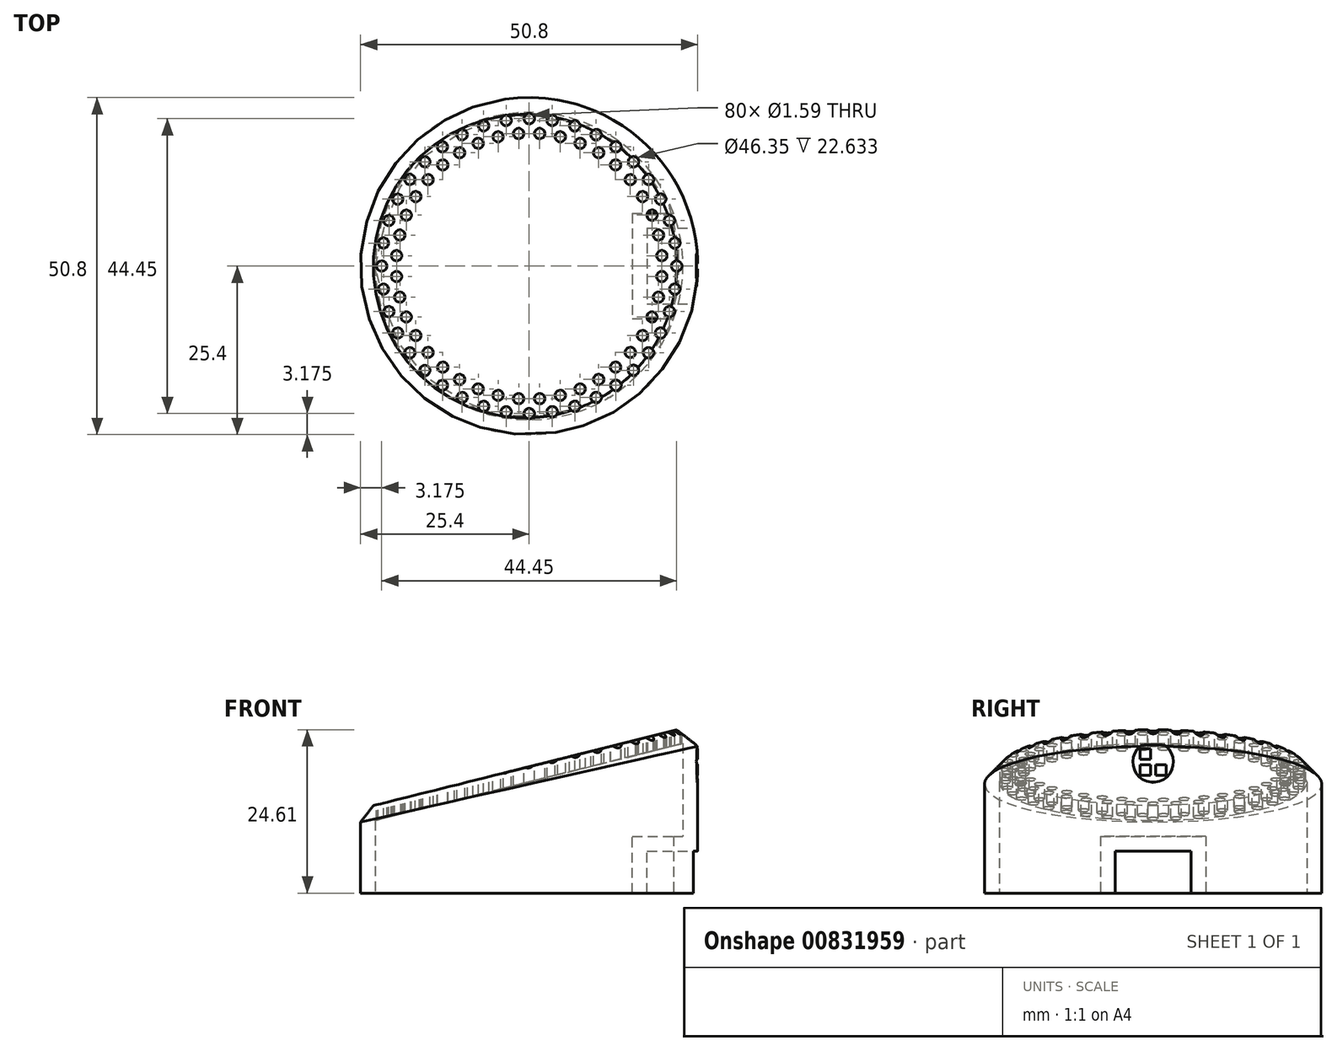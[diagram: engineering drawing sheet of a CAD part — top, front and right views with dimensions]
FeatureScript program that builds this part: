
annotation { "Feature Type Name" : "Feature", "Feature Type Description" : "" }
export const myFeature = defineFeature(function(context is Context, id is Id, definition is map)
    precondition{}
    {
        {
            var Q0;
            Q0=qCreatedBy(makeId("Front.planeOp"),FACE);
            var sketch = newSketch(context, id + "F0", { "sketchPlane" : qUnion([Q0])});
            skLineSegment(sketch, "E0", {"start": v(25.4, 0) * mm, "end": v(25.4, 25.4) * mm});
            skLineSegment(sketch, "E1", {"start": v(25.4, 25.4) * mm, "end": v(-25.4, 12.7) * mm});
            skLineSegment(sketch, "E2", {"start": v(-25.4, 12.7) * mm, "end": v(-25.4, 0) * mm});
            skLineSegment(sketch, "E3", {"start": v(-25.4, 0) * mm, "end": v(25.4, 0) * mm});
            skSolve(sketch);
        }
        {
            var Q0;
            Q0 = qSketchRegion(id + "F0", true);
            extrude(context, id + "F1", {"entities" : qUnion([Q0]), "endBound" : BoundingType.SYMMETRIC, "depth" : 50.8 * mm, "offsetDistance" : 25.4 * mm});
        }
        {
            var Q0;
            Q0=qCreatedBy(makeId("Top.planeOp"),FACE);
            var sketch = newSketch(context, id + "F2", { "sketchPlane" : qUnion([Q0])});
            skCircle(sketch, "E4", {"center": v(0, 0) * mm, "radius": 25.4 * mm});
            skLineSegment(sketch, "E5.bottom", {"start": v(25.4, -25.4) * mm, "end": v(-25.4, -25.4) * mm});
            skLineSegment(sketch, "E5.top", {"start": v(25.4, 25.4) * mm, "end": v(-25.4, 25.4) * mm});
            skLineSegment(sketch, "E5.left", {"start": v(25.4, -25.4) * mm, "end": v(25.4, 25.4) * mm});
            skLineSegment(sketch, "E5.right", {"start": v(-25.4, -25.4) * mm, "end": v(-25.4, 25.4) * mm});
            skSolve(sketch);
        }
        {
            var Q0;
            {var subQ0=sQuery(id+"F2.wireOp",EDGE,"E5.right");var subQ1=sQuery(id+"F2.wireOp",EDGE,"E4");var subQ2=makeQuery(id+"F2.imprint","INTERSECT",VERTEX,{"derivedFrom":[subQ1,subQ0]});Q0=makeQuery(id+"F2.imprint","IMPRINT",FACE,{"disambiguationData":[TD([[makeQuery(id+"F2.imprint","IMPRINT",EDGE,{"disambiguationData":[TD([[subQ2,-1.0]])],"derivedFrom":subQ1}),-1.0]])]});}
            var Q1;
            {var subQ0=sQuery(id+"F2.wireOp",EDGE,"E5.left");var subQ1=sQuery(id+"F2.wireOp",EDGE,"E4");var subQ2=makeQuery(id+"F2.imprint","INTERSECT",VERTEX,{"derivedFrom":[subQ1,subQ0]});Q1=makeQuery(id+"F2.imprint","IMPRINT",FACE,{"disambiguationData":[TD([[makeQuery(id+"F2.imprint","IMPRINT",EDGE,{"disambiguationData":[TD([[subQ2,1.0]])],"derivedFrom":subQ1}),-1.0]])]});}
            var Q2;
            {var subQ0=sQuery(id+"F2.wireOp",EDGE,"E5.top");var subQ1=sQuery(id+"F2.wireOp",EDGE,"E4");var subQ2=makeQuery(id+"F2.imprint","INTERSECT",VERTEX,{"derivedFrom":[subQ1,subQ0]});Q2=makeQuery(id+"F2.imprint","IMPRINT",FACE,{"disambiguationData":[TD([[makeQuery(id+"F2.imprint","IMPRINT",EDGE,{"disambiguationData":[TD([[subQ2,1.0]])],"derivedFrom":subQ1}),-1.0]])]});}
            var Q3;
            {var subQ0=sQuery(id+"F2.wireOp",EDGE,"E5.top");var subQ1=sQuery(id+"F2.wireOp",EDGE,"E4");var subQ2=makeQuery(id+"F2.imprint","INTERSECT",VERTEX,{"derivedFrom":[subQ1,subQ0]});Q3=makeQuery(id+"F2.imprint","IMPRINT",FACE,{"disambiguationData":[TD([[makeQuery(id+"F2.imprint","IMPRINT",EDGE,{"disambiguationData":[TD([[subQ2,-1.0]])],"derivedFrom":subQ1}),-1.0]])]});}
            extrude(context, id + "F3", {"entities" : qUnion([Q0, Q1, Q2, Q3]), "operationType" : NewBodyOperationType.REMOVE, "endBound" : BoundingType.THROUGH_ALL, "depth" : 76.2 * mm, "offsetDistance" : 25.4 * mm});
        }
        {
            var Q0;
            Q0=qCreatedBy(makeId("Right.planeOp"),FACE);
            cPlane(context, id + "F4", {"entities" : qUnion([Q0]), "cplaneType" : CPlaneType.OFFSET, "offset" : 25.4 * mm, "width" : 152.4 * mm, "height" : 152.4 * mm});
        }
        {
            var Q0;
            Q0=qCreatedBy(id+"F4.planeOp",FACE);
            var sketch = newSketch(context, id + "F5", { "sketchPlane" : qUnion([Q0])});
            skLineSegment(sketch, "E6.bottom", {"start": v(5.72, 0) * mm, "end": v(-5.72, 0) * mm});
            skLineSegment(sketch, "E6.top", {"start": v(5.72, 6.35) * mm, "end": v(-5.72, 6.35) * mm});
            skLineSegment(sketch, "E6.left", {"start": v(5.71, 0) * mm, "end": v(5.71, 6.35) * mm});
            skLineSegment(sketch, "E6.right", {"start": v(-5.72, 0) * mm, "end": v(-5.72, 6.35) * mm});
            skLineSegment(sketch, "E7", {"start": v(0, 0) * mm, "end": v(0, 6.35) * mm, "construction": true});
            skSolve(sketch);
        }
        {
            var Q0;
            Q0 = qSketchRegion(id + "F5", true);
            extrude(context, id + "F6", {"entities" : qUnion([Q0]), "operationType" : NewBodyOperationType.REMOVE, "oppositeDirection" : true, "depth" : 7.62 * mm, "offsetDistance" : 25.4 * mm});
        }
        {
            var Q0;
            Q0=makeQuery(id+"F1.opExtrude","SWEPT_FACE",FACE,{"disambiguationData":[OSD([sQuery(id+"F0.wireOp",EDGE,"E3")])]});
            cPlane(context, id + "F7", {"entities" : qUnion([Q0]), "cplaneType" : CPlaneType.OFFSET, "offset" : 25.4 * mm, "oppositeDirection" : true, "width" : 152.4 * mm, "height" : 152.4 * mm});
        }
        {
            var Q0;
            Q0=qCreatedBy(id+"F7.planeOp",FACE);
            var sketch = newSketch(context, id + "F8", { "sketchPlane" : qUnion([Q0])});
            skCircle(sketch, "E8", {"center": v(0, -22.23) * mm, "radius": 0.8 * mm});
            skLineSegment(sketch, "E9", {"start": v(0, 25.4) * mm, "end": v(0, -25.4) * mm, "construction": true});
            skCircle(sketch, "E10.1.0", {"center": v(3.48, -21.95) * mm, "radius": 0.8 * mm});
            skCircle(sketch, "E10.2.0", {"center": v(6.87, -21.14) * mm, "radius": 0.8 * mm});
            skCircle(sketch, "E10.3.0", {"center": v(10.09, -19.8) * mm, "radius": 0.8 * mm});
            skCircle(sketch, "E10.4.0", {"center": v(13.06, -17.98) * mm, "radius": 0.8 * mm});
            skCircle(sketch, "E10.5.0", {"center": v(15.72, -15.72) * mm, "radius": 0.8 * mm});
            skCircle(sketch, "E10.6.0", {"center": v(17.98, -13.06) * mm, "radius": 0.8 * mm});
            skCircle(sketch, "E10.7.0", {"center": v(19.8, -10.09) * mm, "radius": 0.8 * mm});
            skCircle(sketch, "E10.8.0", {"center": v(21.14, -6.87) * mm, "radius": 0.8 * mm});
            skCircle(sketch, "E10.9.0", {"center": v(21.95, -3.48) * mm, "radius": 0.8 * mm});
            skCircle(sketch, "E10.10.0", {"center": v(22.23, 0) * mm, "radius": 0.8 * mm});
            skCircle(sketch, "E10.11.0", {"center": v(21.95, 3.48) * mm, "radius": 0.8 * mm});
            skCircle(sketch, "E10.12.0", {"center": v(21.14, 6.87) * mm, "radius": 0.8 * mm});
            skCircle(sketch, "E10.13.0", {"center": v(19.8, 10.09) * mm, "radius": 0.8 * mm});
            skCircle(sketch, "E10.14.0", {"center": v(17.98, 13.06) * mm, "radius": 0.8 * mm});
            skCircle(sketch, "E10.15.0", {"center": v(15.72, 15.72) * mm, "radius": 0.8 * mm});
            skCircle(sketch, "E10.16.0", {"center": v(13.06, 17.98) * mm, "radius": 0.8 * mm});
            skCircle(sketch, "E10.17.0", {"center": v(10.09, 19.8) * mm, "radius": 0.8 * mm});
            skCircle(sketch, "E10.18.0", {"center": v(6.87, 21.14) * mm, "radius": 0.8 * mm});
            skCircle(sketch, "E10.19.0", {"center": v(3.48, 21.95) * mm, "radius": 0.8 * mm});
            skPoint(sketch, "E10.center", {"position": v(0, 0) * mm});
            skCircle(sketch, "E11.1.20.0", {"center": v(0, 22.23) * mm, "radius": 0.8 * mm});
            skCircle(sketch, "E11.1.21.0", {"center": v(-3.48, 21.95) * mm, "radius": 0.8 * mm});
            skCircle(sketch, "E11.1.22.0", {"center": v(-6.87, 21.14) * mm, "radius": 0.8 * mm});
            skCircle(sketch, "E11.1.23.0", {"center": v(-10.09, 19.8) * mm, "radius": 0.8 * mm});
            skCircle(sketch, "E11.1.24.0", {"center": v(-13.06, 17.98) * mm, "radius": 0.8 * mm});
            skCircle(sketch, "E11.1.25.0", {"center": v(-15.72, 15.72) * mm, "radius": 0.8 * mm});
            skCircle(sketch, "E11.1.26.0", {"center": v(-17.98, 13.06) * mm, "radius": 0.8 * mm});
            skCircle(sketch, "E11.1.27.0", {"center": v(-19.8, 10.09) * mm, "radius": 0.8 * mm});
            skCircle(sketch, "E11.1.28.0", {"center": v(-21.14, 6.87) * mm, "radius": 0.8 * mm});
            skCircle(sketch, "E11.1.29.0", {"center": v(-21.95, 3.48) * mm, "radius": 0.8 * mm});
            skCircle(sketch, "E11.1.30.0", {"center": v(-22.23, 0) * mm, "radius": 0.8 * mm});
            skCircle(sketch, "E11.1.31.0", {"center": v(-21.95, -3.48) * mm, "radius": 0.8 * mm});
            skCircle(sketch, "E11.1.32.0", {"center": v(-21.14, -6.87) * mm, "radius": 0.8 * mm});
            skCircle(sketch, "E11.1.33.0", {"center": v(-19.8, -10.09) * mm, "radius": 0.8 * mm});
            skCircle(sketch, "E11.1.34.0", {"center": v(-17.98, -13.06) * mm, "radius": 0.8 * mm});
            skCircle(sketch, "E11.1.35.0", {"center": v(-15.72, -15.72) * mm, "radius": 0.8 * mm});
            skCircle(sketch, "E11.1.36.0", {"center": v(-13.06, -17.98) * mm, "radius": 0.8 * mm});
            skCircle(sketch, "E11.1.37.0", {"center": v(-10.09, -19.8) * mm, "radius": 0.8 * mm});
            skCircle(sketch, "E11.1.38.0", {"center": v(-6.87, -21.14) * mm, "radius": 0.8 * mm});
            skCircle(sketch, "E11.1.39.0", {"center": v(-3.48, -21.95) * mm, "radius": 0.8 * mm});
            skSolve(sketch);
        }
        {
            var Q0;
            Q0=makeQuery(id+"F1.opExtrude","SWEPT_FACE",FACE,{"disambiguationData":[OSD([sQuery(id+"F0.wireOp",EDGE,"E3")])]});
            shell(context, id + "F9", {"entities" : qUnion([Q0]), "thickness" : 2.22 * mm});
        }
        {
            var Q0;
            Q0 = qSketchRegion(id + "F8", true);
            var Q1;
            Q1=makeQuery(id+"F9.opShell","OFFSET_FACE",FACE,{"disambiguationData":[OSD([sQuery(id+"F0.wireOp",EDGE,"E1")])]});
            var Q2;
            Q2=makeQuery(id+"F9.opShell","OFFSET_VERTEX",VERTEX,{"disambiguationData":[OSD([sQuery(id+"F5.wireOp",EDGE,"E6.top"),sQuery(id+"F5.wireOp",EDGE,"E6.right")])]});
            extrude(context, id + "F10", {"entities" : qUnion([Q0, Q1]), "operationType" : NewBodyOperationType.REMOVE, "endBound" : BoundingType.UP_TO_VERTEX, "depth" : 25.4 * mm, "endBoundEntityVertex" : qUnion([Q2]), "offsetDistance" : 25.4 * mm});
        }
        {
            var Q0;
            Q0=qCreatedBy(id+"F7.planeOp",FACE);
            var sketch = newSketch(context, id + "F11", { "sketchPlane" : qUnion([Q0])});
            skCircle(sketch, "E12", {"center": v(19.98, 1.57) * mm, "radius": 0.8 * mm});
            skLineSegment(sketch, "E13", {"start": v(0, 0) * mm, "end": v(22.23, 0) * mm, "construction": true});
            skLineSegment(sketch, "E14", {"start": v(21.95, 3.48) * mm, "end": v(0, 0) * mm, "construction": true});
            skLineSegment(sketch, "E15", {"start": v(21.95, 3.48) * mm, "end": v(22.23, 0) * mm, "construction": true});
            skLineSegment(sketch, "E16", {"start": v(22.09, 1.74) * mm, "end": v(0, 0) * mm, "construction": true});
            skCircle(sketch, "E17.1.0", {"center": v(19.49, 4.68) * mm, "radius": 0.8 * mm});
            skCircle(sketch, "E17.2.0", {"center": v(18.51, 7.67) * mm, "radius": 0.8 * mm});
            skPoint(sketch, "E17.center", {"position": v(0, 0) * mm});
            skCircle(sketch, "E18.1.3.0", {"center": v(17.09, 10.47) * mm, "radius": 0.8 * mm});
            skCircle(sketch, "E18.1.4.0", {"center": v(15.24, 13.01) * mm, "radius": 0.8 * mm});
            skCircle(sketch, "E18.1.5.0", {"center": v(13.01, 15.24) * mm, "radius": 0.8 * mm});
            skCircle(sketch, "E18.1.6.0", {"center": v(10.47, 17.09) * mm, "radius": 0.8 * mm});
            skCircle(sketch, "E18.1.7.0", {"center": v(7.67, 18.51) * mm, "radius": 0.8 * mm});
            skCircle(sketch, "E18.1.8.0", {"center": v(4.68, 19.49) * mm, "radius": 0.8 * mm});
            skCircle(sketch, "E18.1.9.0", {"center": v(1.57, 19.98) * mm, "radius": 0.8 * mm});
            skCircle(sketch, "E18.1.10.0", {"center": v(-1.57, 19.98) * mm, "radius": 0.8 * mm});
            skCircle(sketch, "E18.1.11.0", {"center": v(-4.68, 19.49) * mm, "radius": 0.8 * mm});
            skCircle(sketch, "E18.1.12.0", {"center": v(-7.67, 18.51) * mm, "radius": 0.8 * mm});
            skCircle(sketch, "E18.1.13.0", {"center": v(-10.47, 17.09) * mm, "radius": 0.8 * mm});
            skCircle(sketch, "E18.1.14.0", {"center": v(-13.01, 15.24) * mm, "radius": 0.8 * mm});
            skCircle(sketch, "E18.1.15.0", {"center": v(-15.24, 13.01) * mm, "radius": 0.8 * mm});
            skCircle(sketch, "E18.1.16.0", {"center": v(-17.09, 10.47) * mm, "radius": 0.8 * mm});
            skCircle(sketch, "E18.1.17.0", {"center": v(-18.51, 7.67) * mm, "radius": 0.8 * mm});
            skCircle(sketch, "E18.1.18.0", {"center": v(-19.49, 4.68) * mm, "radius": 0.8 * mm});
            skCircle(sketch, "E18.1.19.0", {"center": v(-19.98, 1.57) * mm, "radius": 0.8 * mm});
            skCircle(sketch, "E18.1.20.0", {"center": v(-19.98, -1.57) * mm, "radius": 0.8 * mm});
            skCircle(sketch, "E18.1.21.0", {"center": v(-19.49, -4.68) * mm, "radius": 0.8 * mm});
            skCircle(sketch, "E18.1.22.0", {"center": v(-18.51, -7.67) * mm, "radius": 0.8 * mm});
            skCircle(sketch, "E18.1.23.0", {"center": v(-17.09, -10.47) * mm, "radius": 0.8 * mm});
            skCircle(sketch, "E18.1.24.0", {"center": v(-15.24, -13.01) * mm, "radius": 0.8 * mm});
            skCircle(sketch, "E18.1.25.0", {"center": v(-13.01, -15.24) * mm, "radius": 0.8 * mm});
            skCircle(sketch, "E18.1.26.0", {"center": v(-10.47, -17.09) * mm, "radius": 0.8 * mm});
            skCircle(sketch, "E18.1.27.0", {"center": v(-7.67, -18.51) * mm, "radius": 0.8 * mm});
            skCircle(sketch, "E18.1.28.0", {"center": v(-4.68, -19.49) * mm, "radius": 0.8 * mm});
            skCircle(sketch, "E18.1.29.0", {"center": v(-1.57, -19.98) * mm, "radius": 0.8 * mm});
            skCircle(sketch, "E18.1.30.0", {"center": v(1.57, -19.98) * mm, "radius": 0.8 * mm});
            skCircle(sketch, "E18.1.31.0", {"center": v(4.68, -19.49) * mm, "radius": 0.8 * mm});
            skCircle(sketch, "E18.1.32.0", {"center": v(7.67, -18.51) * mm, "radius": 0.8 * mm});
            skCircle(sketch, "E18.1.33.0", {"center": v(10.47, -17.09) * mm, "radius": 0.8 * mm});
            skCircle(sketch, "E18.1.34.0", {"center": v(13.01, -15.24) * mm, "radius": 0.8 * mm});
            skCircle(sketch, "E18.1.35.0", {"center": v(15.24, -13.01) * mm, "radius": 0.8 * mm});
            skCircle(sketch, "E18.1.36.0", {"center": v(17.09, -10.47) * mm, "radius": 0.8 * mm});
            skCircle(sketch, "E18.1.37.0", {"center": v(18.51, -7.67) * mm, "radius": 0.8 * mm});
            skCircle(sketch, "E18.1.38.0", {"center": v(19.49, -4.68) * mm, "radius": 0.8 * mm});
            skCircle(sketch, "E19.1.39.0", {"center": v(19.98, -1.57) * mm, "radius": 0.8 * mm});
            skSolve(sketch);
        }
        {
            var Q0;
            Q0 = qSketchRegion(id + "F11", true);
            var Q1;
            Q1=makeQuery(id+"F9.opShell","OFFSET_FACE",FACE,{"disambiguationData":[OSD([sQuery(id+"F5.wireOp",EDGE,"E6.top")])]});
            extrude(context, id + "F12", {"entities" : qUnion([Q0]), "operationType" : NewBodyOperationType.REMOVE, "endBound" : BoundingType.UP_TO_SURFACE, "depth" : 25.4 * mm, "endBoundEntityFace" : qUnion([Q1]), "offsetDistance" : 25.4 * mm});
        }
        {
            var Q0;
            Q0=qCreatedBy(id+"F4.planeOp",FACE);
            var sketch = newSketch(context, id + "F13", { "sketchPlane" : qUnion([Q0])});
            skLineSegment(sketch, "E20.bottom", {"start": v(-1.98, 21.75) * mm, "end": v(-0.4, 21.75) * mm});
            skLineSegment(sketch, "E20.top", {"start": v(-1.98, 20.16) * mm, "end": v(-0.4, 20.16) * mm});
            skLineSegment(sketch, "E20.left", {"start": v(-1.98, 21.75) * mm, "end": v(-1.98, 20.16) * mm});
            skLineSegment(sketch, "E20.right", {"start": v(-0.4, 21.75) * mm, "end": v(-0.4, 20.16) * mm});
            skLineSegment(sketch, "E21.bottom", {"start": v(-1.98, 19.37) * mm, "end": v(-0.4, 19.37) * mm});
            skLineSegment(sketch, "E21.top", {"start": v(-1.98, 17.78) * mm, "end": v(-0.4, 17.78) * mm});
            skLineSegment(sketch, "E21.left", {"start": v(-1.98, 19.37) * mm, "end": v(-1.98, 17.78) * mm});
            skLineSegment(sketch, "E21.right", {"start": v(-0.4, 19.37) * mm, "end": v(-0.4, 17.78) * mm});
            skLineSegment(sketch, "E22.bottom", {"start": v(0.4, 17.78) * mm, "end": v(1.98, 17.78) * mm});
            skLineSegment(sketch, "E22.top", {"start": v(0.4, 19.37) * mm, "end": v(1.98, 19.37) * mm});
            skLineSegment(sketch, "E22.left", {"start": v(0.4, 19.37) * mm, "end": v(0.4, 17.78) * mm});
            skLineSegment(sketch, "E22.right", {"start": v(1.98, 19.37) * mm, "end": v(1.98, 17.78) * mm});
            skLineSegment(sketch, "E23", {"start": v(0.4, 17.78) * mm, "end": v(-0.4, 17.78) * mm, "construction": true});
            skLineSegment(sketch, "E24", {"start": v(-0.4, 19.37) * mm, "end": v(-0.4, 20.16) * mm, "construction": true});
            skLineSegment(sketch, "E25", {"start": v(0, 17.78) * mm, "end": v(0, 0) * mm, "construction": true});
            skCircle(sketch, "E26", {"center": v(0, 19.76) * mm, "radius": 3.06 * mm});
            skLineSegment(sketch, "E27", {"start": v(0, 17.78) * mm, "end": v(0, 19.76) * mm});
            skLineSegment(sketch, "E28", {"start": v(-0.4, 19.76) * mm, "end": v(0, 19.76) * mm, "construction": true});
            skSolve(sketch);
        }
        {
            var Q0;
            Q0 = qSketchRegion(id + "F13", true);
            extrude(context, id + "F14", {"entities" : qUnion([Q0]), "operationType" : NewBodyOperationType.REMOVE, "oppositeDirection" : true, "depth" : 0.24 * mm, "offsetDistance" : 25.4 * mm});
        }
        {
            var Q0;
            {var subQ0=sQuery(id+"F2.wireOp",EDGE,"E4");var subQ1=makeQuery(id+"F2.imprint","INTERSECT",VERTEX,{"derivedFrom":[subQ0,sQuery(id+"F2.wireOp",EDGE,"E5.left")]});var subQ3=makeQuery(id+"F2.imprint","INTERSECT",VERTEX,{"derivedFrom":[subQ0,sQuery(id+"F2.wireOp",EDGE,"E5.right")]});var subQ4=makeQuery(id+"F2.imprint","INTERSECT",VERTEX,{"derivedFrom":[subQ0,sQuery(id+"F2.wireOp",EDGE,"E5.top")]});Q0=makeQuery(id+"F3.boolean.opBoolean","INTERSECT",EDGE,{"derivedFrom":[makeQuery(id+"F1.opExtrude","SWEPT_FACE",FACE,{"disambiguationData":[OSD([sQuery(id+"F0.wireOp",EDGE,"E1")])]}),makeQuery(id+"F3.opExtrude","SWEPT_FACE",FACE,{"disambiguationData":[OSD([subQ0]),TDD([makeQuery(id+"F2.imprint","IMPRINT",EDGE,{"disambiguationData":[TD([[subQ4,1.0]])],"derivedFrom":subQ0})])]}),makeQuery(id+"F3.opExtrude","SWEPT_FACE",FACE,{"disambiguationData":[OSD([subQ0]),TDD([makeQuery(id+"F2.imprint","IMPRINT",EDGE,{"disambiguationData":[TD([[subQ4,-1.0]])],"derivedFrom":subQ0})])]}),makeQuery(id+"F3.opExtrude","SWEPT_FACE",FACE,{"disambiguationData":[OSD([subQ0]),TDD([makeQuery(id+"F2.imprint","IMPRINT",EDGE,{"disambiguationData":[TD([[subQ3,-1.0]])],"derivedFrom":subQ0})])]}),makeQuery(id+"F3.opExtrude","SWEPT_FACE",FACE,{"disambiguationData":[OSD([subQ0]),TDD([makeQuery(id+"F2.imprint","IMPRINT",EDGE,{"disambiguationData":[TD([[subQ1,1.0]])],"derivedFrom":subQ0})])]})]});}
            chamfer(context, id + "F15", {"entities" : qUnion([Q0]), "width" : 2.54 * mm, "tangentPropagation" : true});
        }
    });
